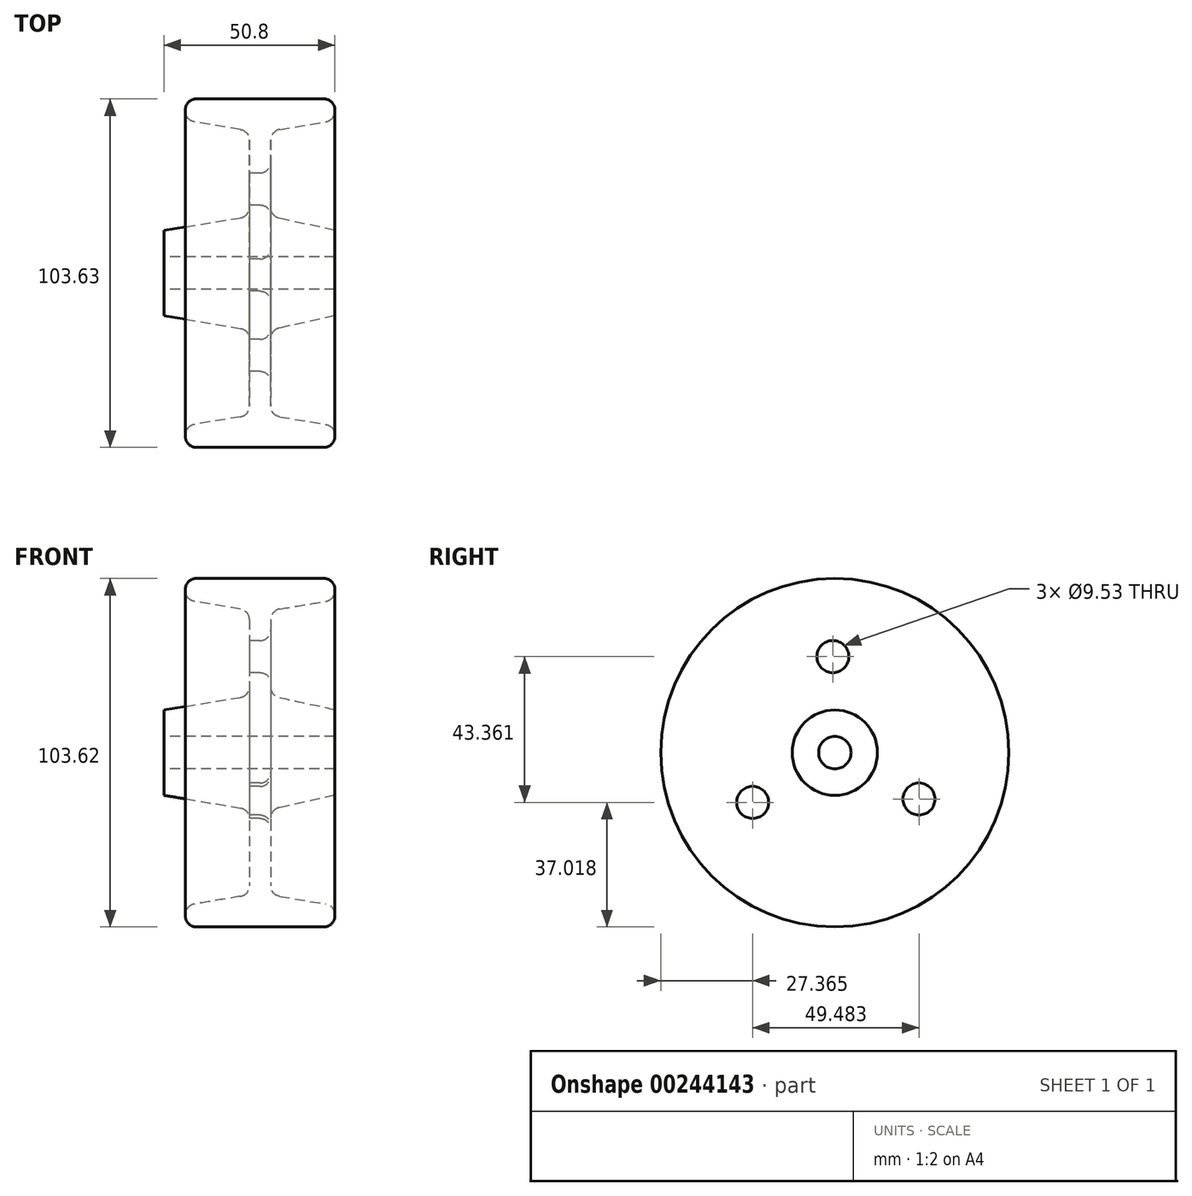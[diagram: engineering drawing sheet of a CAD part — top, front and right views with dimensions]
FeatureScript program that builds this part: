
annotation { "Feature Type Name" : "Feature", "Feature Type Description" : "" }
export const myFeature = defineFeature(function(context is Context, id is Id, definition is map)
    precondition{}
    {
        {
            var Q0;
            Q0=qCreatedBy(makeId("Top.planeOp"),FACE);
            var sketch = newSketch(context, id + "F0", { "sketchPlane" : qUnion([Q0])});
            skLineSegment(sketch, "E0", {"start": v(-25.85, 0) * mm, "end": v(24.95, 0) * mm});
            skLineSegment(sketch, "E1", {"start": v(-25.85, 0) * mm, "end": v(-25.85, 7.87) * mm});
            skLineSegment(sketch, "E2", {"start": v(24.95, 0) * mm, "end": v(24.95, 7.87) * mm});
            skLineSegment(sketch, "E3", {"start": v(-25.85, 7.87) * mm, "end": v(-0.45, 12.06) * mm});
            skLineSegment(sketch, "E4", {"start": v(5.9, 12.06) * mm, "end": v(24.95, 7.87) * mm});
            skLineSegment(sketch, "E5", {"start": v(-0.45, 12.06) * mm, "end": v(-0.45, 37.46) * mm});
            skLineSegment(sketch, "E6", {"start": v(5.9, 12.06) * mm, "end": v(5.9, 37.46) * mm});
            skLineSegment(sketch, "E7", {"start": v(-0.45, 46.99) * mm, "end": v(-19.5, 46.99) * mm});
            skLineSegment(sketch, "E8", {"start": v(-19.5, 46.99) * mm, "end": v(-19.5, 40.64) * mm});
            skLineSegment(sketch, "E9", {"start": v(-19.5, 40.64) * mm, "end": v(-0.45, 37.46) * mm});
            skLineSegment(sketch, "E10", {"start": v(-0.45, 46.99) * mm, "end": v(24.95, 46.99) * mm});
            skLineSegment(sketch, "E11", {"start": v(24.95, 46.99) * mm, "end": v(24.95, 40.64) * mm});
            skLineSegment(sketch, "E12", {"start": v(24.95, 40.64) * mm, "end": v(5.9, 37.46) * mm});
            skLineSegment(sketch, "E13", {"start": v(-25.85, -4.83) * mm, "end": v(25.27, -4.83) * mm, "construction": true});
            skLineSegment(sketch, "E14", {"start": v(-0.45, 46.99) * mm, "end": v(-0.45, 37.46) * mm});
            skLineSegment(sketch, "E15", {"start": v(-0.45, 12.06) * mm, "end": v(5.9, 12.06) * mm});
            skSolve(sketch);
        }
        {
            var Q0;
            Q0 = qSketchRegion(id + "F0", true);
            var Q1;
            Q1=sQuery(id+"F0.wireOp",EDGE,"E13");
            revolve(context, id + "F1", {"entities" : qUnion([Q0]), "axis" : qUnion([Q1]), "revolveType" : RevolveType.FULL});
        }
        {
            var Q0;
            Q0=makeQuery(id+"F1.opRevolve","SWEPT_EDGE",EDGE,{"disambiguationData":[OSD([sQuery(id+"F0.wireOp",EDGE,"E6"),sQuery(id+"F0.wireOp",EDGE,"E12")])]});
            var Q1;
            Q1=makeQuery(id+"F1.opRevolve","SWEPT_EDGE",EDGE,{"disambiguationData":[OSD([sQuery(id+"F0.wireOp",EDGE,"E11"),sQuery(id+"F0.wireOp",EDGE,"E12")])]});
            var Q2;
            Q2=makeQuery(id+"F1.opRevolve","SWEPT_EDGE",EDGE,{"disambiguationData":[OSD([sQuery(id+"F0.wireOp",EDGE,"E10"),sQuery(id+"F0.wireOp",EDGE,"E11")])]});
            var Q3;
            Q3=makeQuery(id+"F1.opRevolve","SWEPT_EDGE",EDGE,{"disambiguationData":[OSD([sQuery(id+"F0.wireOp",EDGE,"E4"),sQuery(id+"F0.wireOp",EDGE,"E6"),sQuery(id+"F0.wireOp",EDGE,"E15")])]});
            var Q4;
            Q4=makeQuery(id+"F1.opRevolve","SWEPT_EDGE",EDGE,{"disambiguationData":[OSD([sQuery(id+"F0.wireOp",EDGE,"E7"),sQuery(id+"F0.wireOp",EDGE,"E8")])]});
            var Q5;
            Q5=makeQuery(id+"F1.opRevolve","SWEPT_EDGE",EDGE,{"disambiguationData":[OSD([sQuery(id+"F0.wireOp",EDGE,"E8"),sQuery(id+"F0.wireOp",EDGE,"E9")])]});
            var Q6;
            Q6=makeQuery(id+"F1.opRevolve","SWEPT_EDGE",EDGE,{"disambiguationData":[OSD([sQuery(id+"F0.wireOp",EDGE,"E3"),sQuery(id+"F0.wireOp",EDGE,"E5"),sQuery(id+"F0.wireOp",EDGE,"E15")])]});
            var Q7;
            Q7=makeQuery(id+"F1.opRevolve","SWEPT_EDGE",EDGE,{"disambiguationData":[OSD([sQuery(id+"F0.wireOp",EDGE,"E5"),sQuery(id+"F0.wireOp",EDGE,"E9"),sQuery(id+"F0.wireOp",EDGE,"E14")])]});
            fillet(context, id + "F2", {"entities" : qUnion([Q0, Q1, Q2, Q3, Q4, Q5, Q6, Q7]), "radius" : 3.17 * mm, "tangentPropagation" : true, "allowEdgeOverflow" : false});
        }
        {
            var Q0;
            Q0=makeQuery(id+"F1.opRevolve","SWEPT_FACE",FACE,{"disambiguationData":[OSD([sQuery(id+"F0.wireOp",EDGE,"E5")])]});
            var sketch = newSketch(context, id + "F3", { "sketchPlane" : qUnion([Q0])});
            skCircle(sketch, "E16", {"center": v(4.83, 0) * mm, "radius": 28.57 * mm});
            skCircle(sketch, "E17", {"center": v(5.41, 28.57) * mm, "radius": 4.76 * mm});
            skCircle(sketch, "E18.1.0", {"center": v(-20.2, -13.78) * mm, "radius": 4.76 * mm});
            skCircle(sketch, "E18.2.0", {"center": v(29.27, -14.8) * mm, "radius": 4.76 * mm});
            skSolve(sketch);
        }
        {
            var Q0;
            {var subQ0=sQuery(id+"F3.wireOp",EDGE,"E17");var subQ1=sQuery(id+"F3.wireOp",EDGE,"E16");var subQ2=makeQuery(id+"F3.imprint","INTERSECT",VERTEX,{"disambiguationData":[OD(0.0)],"derivedFrom":[subQ1,subQ0]});Q0=makeQuery(id+"F3.imprint","IMPRINT",FACE,{"disambiguationData":[TD([[makeQuery(id+"F3.imprint","IMPRINT",EDGE,{"disambiguationData":[TD([[subQ2,1.0]])],"derivedFrom":subQ1}),1.0]])]});}
            var Q1;
            {var subQ0=sQuery(id+"F3.wireOp",EDGE,"E17");var subQ1=sQuery(id+"F3.wireOp",EDGE,"E16");var subQ2=makeQuery(id+"F3.imprint","INTERSECT",VERTEX,{"disambiguationData":[OD(0.0)],"derivedFrom":[subQ1,subQ0]});Q1=makeQuery(id+"F3.imprint","IMPRINT",FACE,{"disambiguationData":[TD([[makeQuery(id+"F3.imprint","IMPRINT",EDGE,{"disambiguationData":[TD([[subQ2,1.0]])],"derivedFrom":subQ1}),-1.0]])]});}
            var Q2;
            {var subQ0=sQuery(id+"F3.wireOp",EDGE,"E18.1.0");var subQ1=sQuery(id+"F3.wireOp",EDGE,"E16");var subQ2=makeQuery(id+"F3.imprint","INTERSECT",VERTEX,{"disambiguationData":[OD(0.0)],"derivedFrom":[subQ1,subQ0]});Q2=makeQuery(id+"F3.imprint","IMPRINT",FACE,{"disambiguationData":[TD([[makeQuery(id+"F3.imprint","IMPRINT",EDGE,{"disambiguationData":[TD([[subQ2,-1.0]])],"derivedFrom":subQ1}),-1.0]])]});}
            var Q3;
            {var subQ0=sQuery(id+"F3.wireOp",EDGE,"E18.2.0");var subQ1=sQuery(id+"F3.wireOp",EDGE,"E16");var subQ2=makeQuery(id+"F3.imprint","INTERSECT",VERTEX,{"disambiguationData":[OD(0.0)],"derivedFrom":[subQ1,subQ0]});Q3=makeQuery(id+"F3.imprint","IMPRINT",FACE,{"disambiguationData":[TD([[makeQuery(id+"F3.imprint","IMPRINT",EDGE,{"disambiguationData":[TD([[subQ2,-1.0]])],"derivedFrom":subQ1}),1.0]])]});}
            var Q4;
            {var subQ0=sQuery(id+"F3.wireOp",EDGE,"E18.2.0");var subQ1=sQuery(id+"F3.wireOp",EDGE,"E16");var subQ2=makeQuery(id+"F3.imprint","INTERSECT",VERTEX,{"disambiguationData":[OD(0.0)],"derivedFrom":[subQ1,subQ0]});Q4=makeQuery(id+"F3.imprint","IMPRINT",FACE,{"disambiguationData":[TD([[makeQuery(id+"F3.imprint","IMPRINT",EDGE,{"disambiguationData":[TD([[subQ2,-1.0]])],"derivedFrom":subQ1}),-1.0]])]});}
            var Q5;
            {var subQ0=sQuery(id+"F3.wireOp",EDGE,"E18.1.0");var subQ1=sQuery(id+"F3.wireOp",EDGE,"E16");var subQ2=makeQuery(id+"F3.imprint","INTERSECT",VERTEX,{"disambiguationData":[OD(0.0)],"derivedFrom":[subQ1,subQ0]});Q5=makeQuery(id+"F3.imprint","IMPRINT",FACE,{"disambiguationData":[TD([[makeQuery(id+"F3.imprint","IMPRINT",EDGE,{"disambiguationData":[TD([[subQ2,-1.0]])],"derivedFrom":subQ1}),1.0]])]});}
            extrude(context, id + "F4", {"entities" : qUnion([Q0, Q1, Q2, Q3, Q4, Q5]), "operationType" : NewBodyOperationType.REMOVE, "oppositeDirection" : true, "depth" : 25.4 * mm});
        }
        {
            var Q0;
            Q0=makeQuery(id+"F4.boolean.opBoolean","COPY",EDGE,{"derivedFrom":makeQuery(id+"F4.opExtrude","CAP_EDGE",EDGE,{"disambiguationData":[OSD([sQuery(id+"F3.wireOp",EDGE,"E18.1.0")])],"isStart":true})});
            var Q1;
            Q1=makeQuery(id+"F4.boolean.opBoolean","INTERSECT",EDGE,{"derivedFrom":[makeQuery(id+"F1.opRevolve","SWEPT_FACE",FACE,{"disambiguationData":[OSD([sQuery(id+"F0.wireOp",EDGE,"E6")])]}),makeQuery(id+"F4.opExtrude","SWEPT_FACE",FACE,{"disambiguationData":[OSD([sQuery(id+"F3.wireOp",EDGE,"E18.1.0")])]})]});
            var Q2;
            Q2=makeQuery(id+"F4.boolean.opBoolean","COPY",EDGE,{"derivedFrom":makeQuery(id+"F4.opExtrude","CAP_EDGE",EDGE,{"disambiguationData":[OSD([sQuery(id+"F3.wireOp",EDGE,"E18.2.0")])],"isStart":true})});
            var Q3;
            Q3=makeQuery(id+"F4.boolean.opBoolean","INTERSECT",EDGE,{"derivedFrom":[makeQuery(id+"F1.opRevolve","SWEPT_FACE",FACE,{"disambiguationData":[OSD([sQuery(id+"F0.wireOp",EDGE,"E6")])]}),makeQuery(id+"F4.opExtrude","SWEPT_FACE",FACE,{"disambiguationData":[OSD([sQuery(id+"F3.wireOp",EDGE,"E18.2.0")])]})]});
            var Q4;
            Q4=makeQuery(id+"F4.boolean.opBoolean","COPY",EDGE,{"derivedFrom":makeQuery(id+"F4.opExtrude","CAP_EDGE",EDGE,{"disambiguationData":[OSD([sQuery(id+"F3.wireOp",EDGE,"E17")])],"isStart":true})});
            var Q5;
            Q5=makeQuery(id+"F4.boolean.opBoolean","INTERSECT",EDGE,{"derivedFrom":[makeQuery(id+"F1.opRevolve","SWEPT_FACE",FACE,{"disambiguationData":[OSD([sQuery(id+"F0.wireOp",EDGE,"E6")])]}),makeQuery(id+"F4.opExtrude","SWEPT_FACE",FACE,{"disambiguationData":[OSD([sQuery(id+"F3.wireOp",EDGE,"E17")])]})]});
            fillet(context, id + "F5", {"entities" : qUnion([Q0, Q1, Q2, Q3, Q4, Q5]), "radius" : 3.17 * mm, "tangentPropagation" : true, "allowEdgeOverflow" : false});
        }
    });
